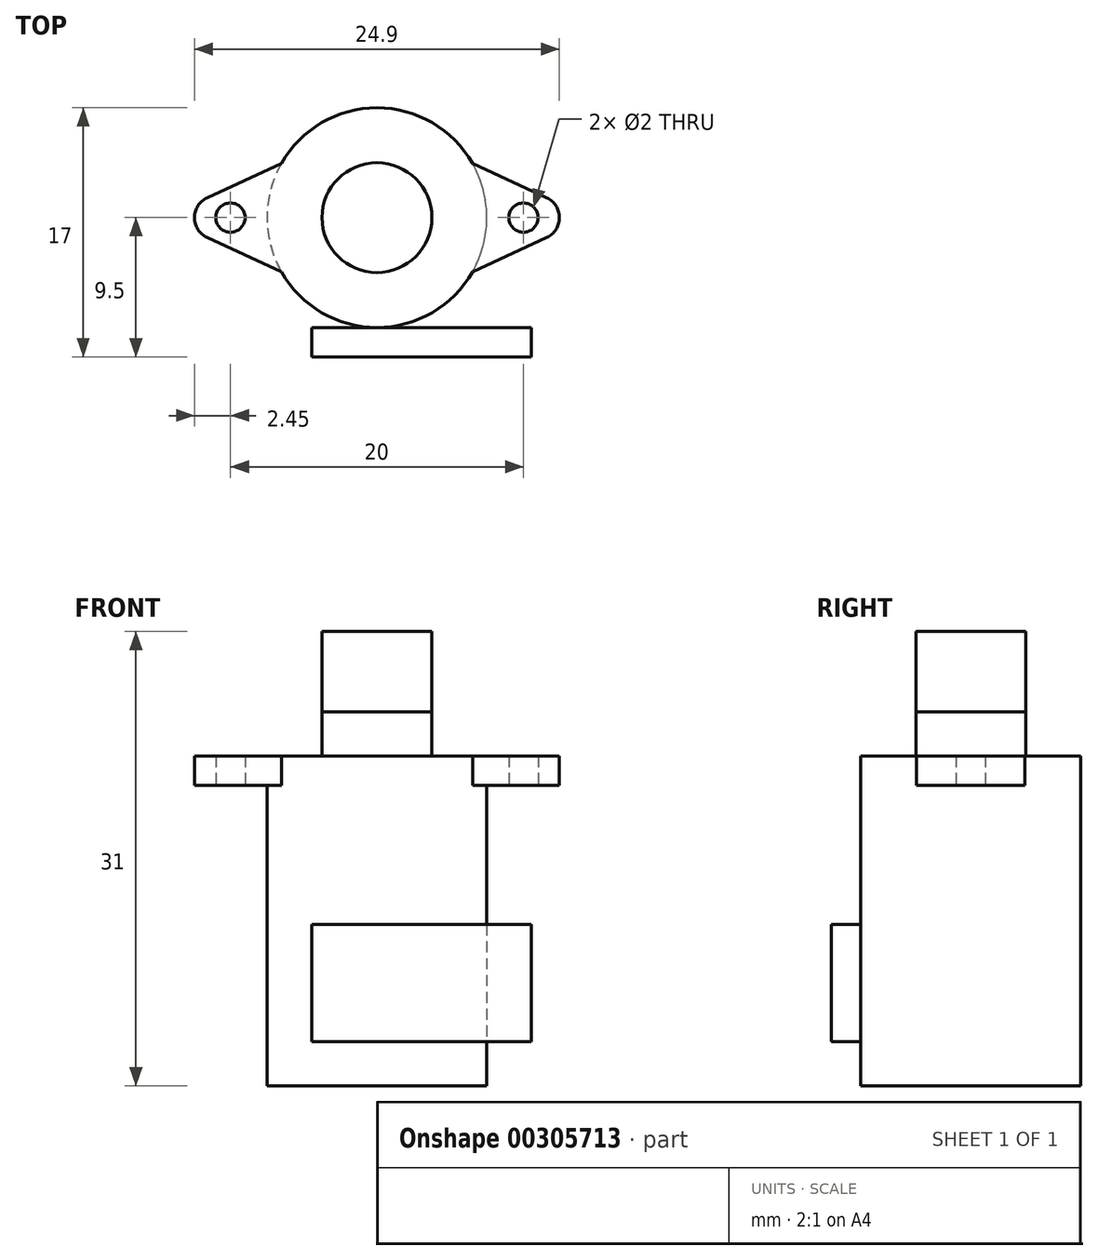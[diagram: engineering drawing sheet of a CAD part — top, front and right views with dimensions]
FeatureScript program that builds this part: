
annotation { "Feature Type Name" : "Feature", "Feature Type Description" : "" }
export const myFeature = defineFeature(function(context is Context, id is Id, definition is map)
    precondition{}
    {
        {
            var Q0;
            Q0=qCreatedBy(makeId("Top.planeOp"),FACE);
            var sketch = newSketch(context, id + "F0", { "sketchPlane" : qUnion([Q0])});
            skCircle(sketch, "E0", {"center": v(0, 0) * mm, "radius": 7.5 * mm});
            skSolve(sketch);
        }
        {
            var Q0;
            Q0=qCreatedBy(makeId("Top.planeOp"),FACE);
            cPlane(context, id + "F1", {"entities" : qUnion([Q0]), "cplaneType" : CPlaneType.OFFSET, "offset" : 11 * mm, "width" : 150 * mm, "height" : 150 * mm});
        }
        {
            var Q0;
            Q0=qCreatedBy(makeId("Top.planeOp"),FACE);
            cPlane(context, id + "F2", {"entities" : qUnion([Q0]), "cplaneType" : CPlaneType.OFFSET, "offset" : 20.5 * mm, "width" : 150 * mm, "height" : 150 * mm});
        }
        {
            var Q0;
            Q0=makeQuery(id+"F0.imprint","IMPRINT",FACE,{"disambiguationData":[TD([[makeQuery(id+"F0.imprint","IMPRINT",EDGE,{"derivedFrom":sQuery(id+"F0.wireOp",EDGE,"E0")}),1.0]])]});
            var Q1;
            Q1=qCreatedBy(id+"F2.planeOp",FACE);
            extrude(context, id + "F3", {"entities" : qUnion([Q0]), "endBound" : BoundingType.UP_TO_SURFACE, "endBoundEntityFace" : qUnion([Q1]), "depth" : 25 * mm});
        }
        {
            var Q0;
            Q0=qCreatedBy(id+"F2.planeOp",FACE);
            var sketch = newSketch(context, id + "F4", { "sketchPlane" : qUnion([Q0])});
            skCircle(sketch, "E1", {"center": v(0, 0) * mm, "radius": 12.45 * mm, "construction": true});
            skLineSegment(sketch, "E2", {"start": v(-24.19, 0) * mm, "end": v(19.11, 0) * mm, "construction": true});
            skLineSegment(sketch, "E3", {"start": v(-23.38, 3.7) * mm, "end": v(18.23, 3.7) * mm, "construction": true});
            skLineSegment(sketch, "E4", {"start": v(-24.36, -3.7) * mm, "end": v(18.76, -3.7) * mm, "construction": true});
            skCircle(sketch, "E5", {"center": v(0, 0) * mm, "radius": 3.75 * mm});
            skPoint(sketch, "E6", {"position": v(-10, 0) * mm});
            skPoint(sketch, "E7", {"position": v(10, 0) * mm});
            skLineSegment(sketch, "E8", {"start": v(0, -15.16) * mm, "end": v(0, 15.16) * mm, "construction": true});
            skCircle(sketch, "E9", {"center": v(-10, 0) * mm, "radius": 1 * mm});
            skCircle(sketch, "E10", {"center": v(10, 0) * mm, "radius": 1 * mm});
            skLineSegment(sketch, "E11", {"start": v(-12.45, 0) * mm, "end": v(-6.52, 3.7) * mm, "construction": true});
            skLineSegment(sketch, "E12", {"start": v(-12.16, 2.65) * mm, "end": v(0, 2.65) * mm, "construction": true});
            skLineSegment(sketch, "E13", {"start": v(-12.16, -2.65) * mm, "end": v(0, -2.65) * mm, "construction": true});
            skLineSegment(sketch, "E14", {"start": v(-10, -2.65) * mm, "end": v(-10, 2.65) * mm, "construction": true});
            skArc(sketch, "E15", {"start": v(-11.58, 1.36) * mm, "mid": v(-12.45, 0) * mm, "end": v(-11.58, -1.36) * mm});
            skLineSegment(sketch, "E16", {"start": v(-11.58, 1.36) * mm, "end": v(-6.52, 3.7) * mm});
            skLineSegment(sketch, "E17", {"start": v(-11.58, -1.36) * mm, "end": v(-6.52, -3.7) * mm});
            skLineSegment(sketch, "E18.MirrorCS", {"start": v(11.58, 1.36) * mm, "end": v(6.52, 3.7) * mm});
            skArc(sketch, "E19.MirrorCS", {"start": v(11.58, 1.36) * mm, "mid": v(12.45, 0) * mm, "end": v(11.58, -1.36) * mm});
            skLineSegment(sketch, "E20.MirrorCS", {"start": v(11.58, -1.36) * mm, "end": v(6.52, -3.7) * mm});
            skCircle(sketch, "E21.0", {"center": v(0, 0) * mm, "radius": 7.5 * mm});
            skSolve(sketch);
        }
        {
            var Q0;
            Q0=makeQuery(id+"F4.imprint","IMPRINT",FACE,{"disambiguationData":[TD([[makeQuery(id+"F4.imprint","IMPRINT",EDGE,{"derivedFrom":sQuery(id+"F4.wireOp",EDGE,"E9")}),-1.0]])]});
            var Q1;
            Q1=makeQuery(id+"F4.imprint","IMPRINT",FACE,{"disambiguationData":[TD([[makeQuery(id+"F4.imprint","IMPRINT",EDGE,{"derivedFrom":sQuery(id+"F4.wireOp",EDGE,"E5")}),-1.0]])]});
            var Q2;
            Q2=makeQuery(id+"F4.imprint","IMPRINT",FACE,{"disambiguationData":[TD([[makeQuery(id+"F4.imprint","IMPRINT",EDGE,{"derivedFrom":sQuery(id+"F4.wireOp",EDGE,"E10")}),-1.0]])]});
            var Q3;
            Q3=makeQuery(id+"F4.imprint","IMPRINT",FACE,{"disambiguationData":[TD([[makeQuery(id+"F4.imprint","IMPRINT",EDGE,{"derivedFrom":sQuery(id+"F4.wireOp",EDGE,"E5")}),1.0]])]});
            extrude(context, id + "F5", {"entities" : qUnion([Q0, Q1, Q2, Q3]), "operationType" : NewBodyOperationType.ADD, "depth" : 2 * mm});
        }
        {
            var Q0;
            Q0=makeQuery(id+"F5.opExtrude","CAP_FACE",FACE,{"disambiguationData":[OSD([sQuery(id+"F4.wireOp",EDGE,"E9"),sQuery(id+"F4.wireOp",EDGE,"E10"),sQuery(id+"F4.wireOp",EDGE,"E15"),sQuery(id+"F4.wireOp",EDGE,"E16"),sQuery(id+"F4.wireOp",EDGE,"E17"),sQuery(id+"F4.wireOp",EDGE,"E18.MirrorCS"),sQuery(id+"F4.wireOp",EDGE,"E19.MirrorCS"),sQuery(id+"F4.wireOp",EDGE,"E20.MirrorCS"),sQuery(id+"F4.wireOp",EDGE,"E21.0")])],"isStart":false});
            var sketch = newSketch(context, id + "F6", { "sketchPlane" : qUnion([Q0])});
            skCircle(sketch, "E22.0", {"center": v(0, 0) * mm, "radius": 3.75 * mm});
            skSolve(sketch);
        }
        {
            var Q0;
            Q0 = qSketchRegion(id + "F6", true);
            extrude(context, id + "F7", {"entities" : qUnion([Q0]), "operationType" : NewBodyOperationType.ADD, "depth" : 3 * mm});
        }
        {
            var Q0;
            Q0=makeQuery(id+"F3.opExtrude","CAP_FACE",FACE,{"disambiguationData":[OSD([sQuery(id+"F0.wireOp",EDGE,"E0")])],"isStart":true});
            var sketch = newSketch(context, id + "F8", { "sketchPlane" : qUnion([Q0])});
            skCircle(sketch, "E23.0", {"center": v(0, 0) * mm, "radius": 3.75 * mm});
            skSolve(sketch);
        }
        {
            var Q0;
            Q0 = qSketchRegion(id + "F8", true);
            extrude(context, id + "F9", {"entities" : qUnion([Q0]), "oppositeDirection" : true, "depth" : 31 * mm});
        }
        {
            var Q0;
            Q0=makeQuery(id+"F3.opExtrude","SWEPT_BODY",BODY,{"disambiguationData":[OSD([sQuery(id+"F0.wireOp",EDGE,"E0")])]});
            var Q1;
            Q1=makeQuery(id+"F9.opExtrude","SWEPT_BODY",BODY,{"disambiguationData":[OSD([sQuery(id+"F8.wireOp",EDGE,"E23.0")])]});
            booleanBodies(context, id + "F10", {"operationType" : BooleanOperationType.SUBTRACTION, "tools" : qUnion([Q0]), "targets" : qUnion([Q1]), "keepTools" : true});
        }
        {
            var Q0;
            Q0=qCreatedBy(id+"F1.planeOp",FACE);
            var sketch = newSketch(context, id + "F11", { "sketchPlane" : qUnion([Q0])});
            skCircle(sketch, "E24", {"center": v(0, 0) * mm, "radius": 7.5 * mm});
            skLineSegment(sketch, "E25", {"start": v(-21.82, -7.5) * mm, "end": v(18.9, -7.5) * mm});
            skSolve(sketch);
        }
        {
            var Q0;
            Q0=sQuery(id+"F11.wireOp",EDGE,"E25");
            cPlane(context, id + "F12", {"entities" : qUnion([Q0]), "cplaneType" : CPlaneType.LINE_ANGLE, "offset" : 25 * mm, "angle" : 0 * degree, "oppositeDirection" : true, "width" : 150 * mm, "height" : 150 * mm});
        }
        {
            var Q0;
            Q0=qCreatedBy(id+"F12.planeOp",FACE);
            var sketch = newSketch(context, id + "F13", { "sketchPlane" : qUnion([Q0])});
            skLineSegment(sketch, "E26.bottom", {"start": v(4.45, 11) * mm, "end": v(-10.55, 11) * mm});
            skLineSegment(sketch, "E26.top", {"start": v(4.45, 3) * mm, "end": v(-10.55, 3) * mm});
            skLineSegment(sketch, "E26.left", {"start": v(4.45, 11) * mm, "end": v(4.45, 3) * mm});
            skLineSegment(sketch, "E26.right", {"start": v(-10.55, 11) * mm, "end": v(-10.55, 3) * mm});
            skLineSegment(sketch, "E27", {"start": v(12.45, 22.5) * mm, "end": v(12.45, 20.5) * mm});
            skSolve(sketch);
        }
        {
            var Q0;
            Q0 = qSketchRegion(id + "F13", true);
            extrude(context, id + "F14", {"entities" : qUnion([Q0]), "operationType" : NewBodyOperationType.ADD, "oppositeDirection" : true, "depth" : 2 * mm});
        }
    });
